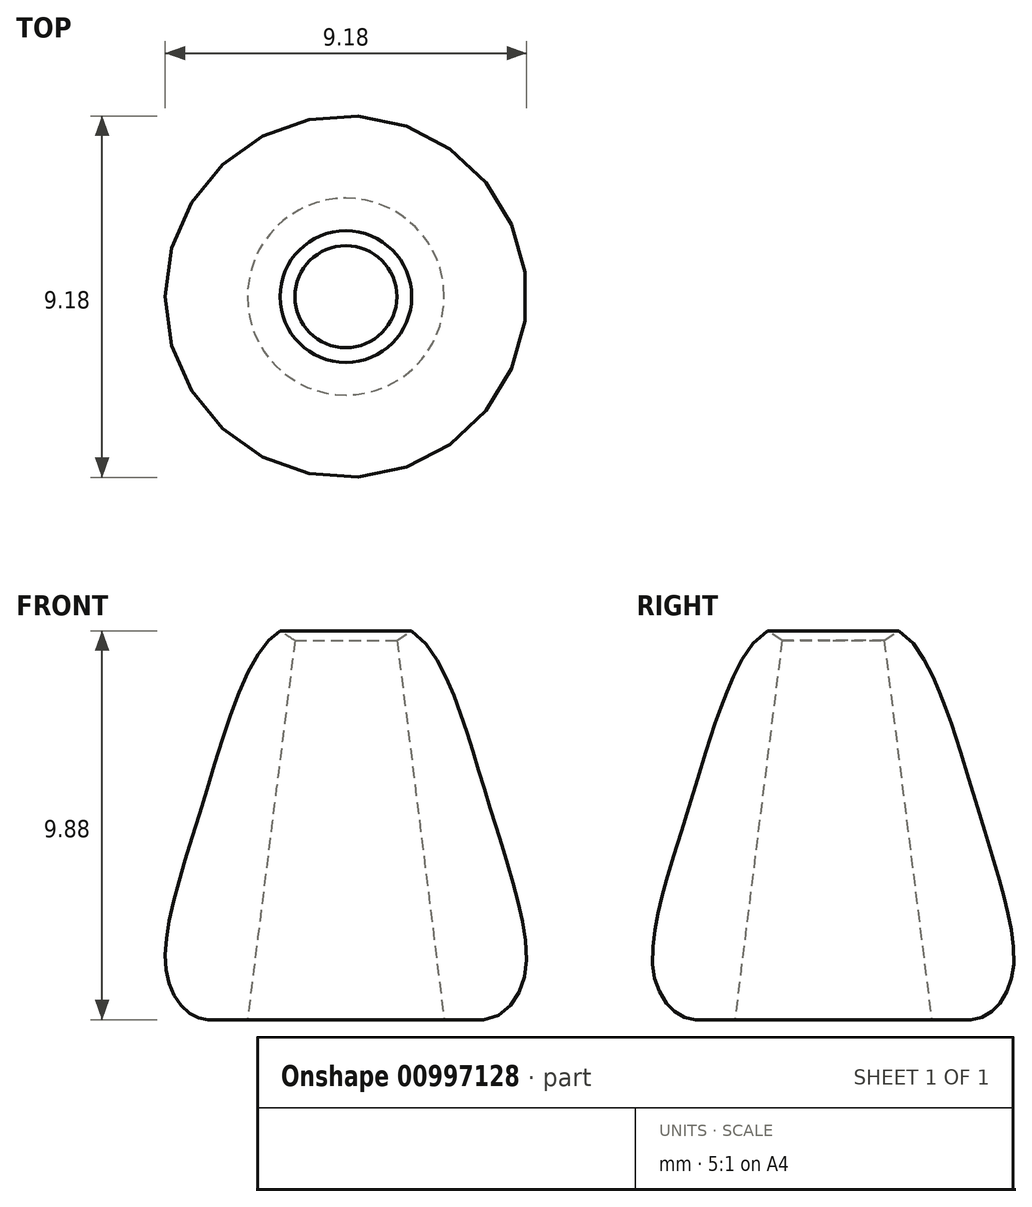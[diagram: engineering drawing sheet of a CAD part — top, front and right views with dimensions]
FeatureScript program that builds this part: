
annotation { "Feature Type Name" : "Feature", "Feature Type Description" : "" }
export const myFeature = defineFeature(function(context is Context, id is Id, definition is map)
    precondition{}
    {
        {
            var Q0;
            Q0=qCreatedBy(makeId("Front.planeOp"),FACE);
            var sketch = newSketch(context, id + "F0", { "sketchPlane" : qUnion([Q0])});
            skLineSegment(sketch, "E0", {"start": v(0, 0) * mm, "end": v(-2.5, 0) * mm});
            skLineSegment(sketch, "E1", {"start": v(-2.5, 0) * mm, "end": v(-3.5, 0) * mm});
            skLineSegment(sketch, "E2", {"start": v(0, 0) * mm, "end": v(0, 10) * mm});
            skLineSegment(sketch, "E3", {"start": v(0, 10) * mm, "end": v(-1.25, 10) * mm});
            skFitSpline(sketch, "E4", {"points": [v(-3.5, 0) * mm, v(-4.5, 0.96) * mm, v(-3.6, 5.6) * mm, v(-1.25, 10) * mm], "startDerivative": vector(-5.84, 0) * mm, "endDerivative": vector(8.3, -0.04) * mm});
            skLineSegment(sketch, "E5", {"start": v(-2.5, 0) * mm, "end": v(-1.25, 10) * mm});
            skSolve(sketch);
        }
        {
            var Q0;
            Q0=makeQuery(id+"F0.imprint","IMPRINT",FACE,{"disambiguationData":[TD([[makeQuery(id+"F0.imprint","IMPRINT",EDGE,{"derivedFrom":sQuery(id+"F0.wireOp",EDGE,"E1")}),-1.0]])]});
            var Q1;
            Q1=sQuery(id+"F0.wireOp",EDGE,"E2");
            revolve(context, id + "F1", {"surfaceOperationType" : NewSurfaceOperationType.NEW, "entities" : qUnion([Q0]), "axis" : qUnion([Q1]), "revolveType" : RevolveType.FULL});
        }
        {
            var Q0;
            Q0=makeQuery(id+"F1.opRevolve","SWEPT_EDGE",EDGE,{"disambiguationData":[OSD([sQuery(id+"F0.wireOp",EDGE,"E3"),sQuery(id+"F0.wireOp",EDGE,"E4"),sQuery(id+"F0.wireOp",EDGE,"E5")])]});
            chamfer(context, id + "F2", {"entities" : qUnion([Q0]), "width" : .25 * mm, "tangentPropagation" : true});
        }
    });
